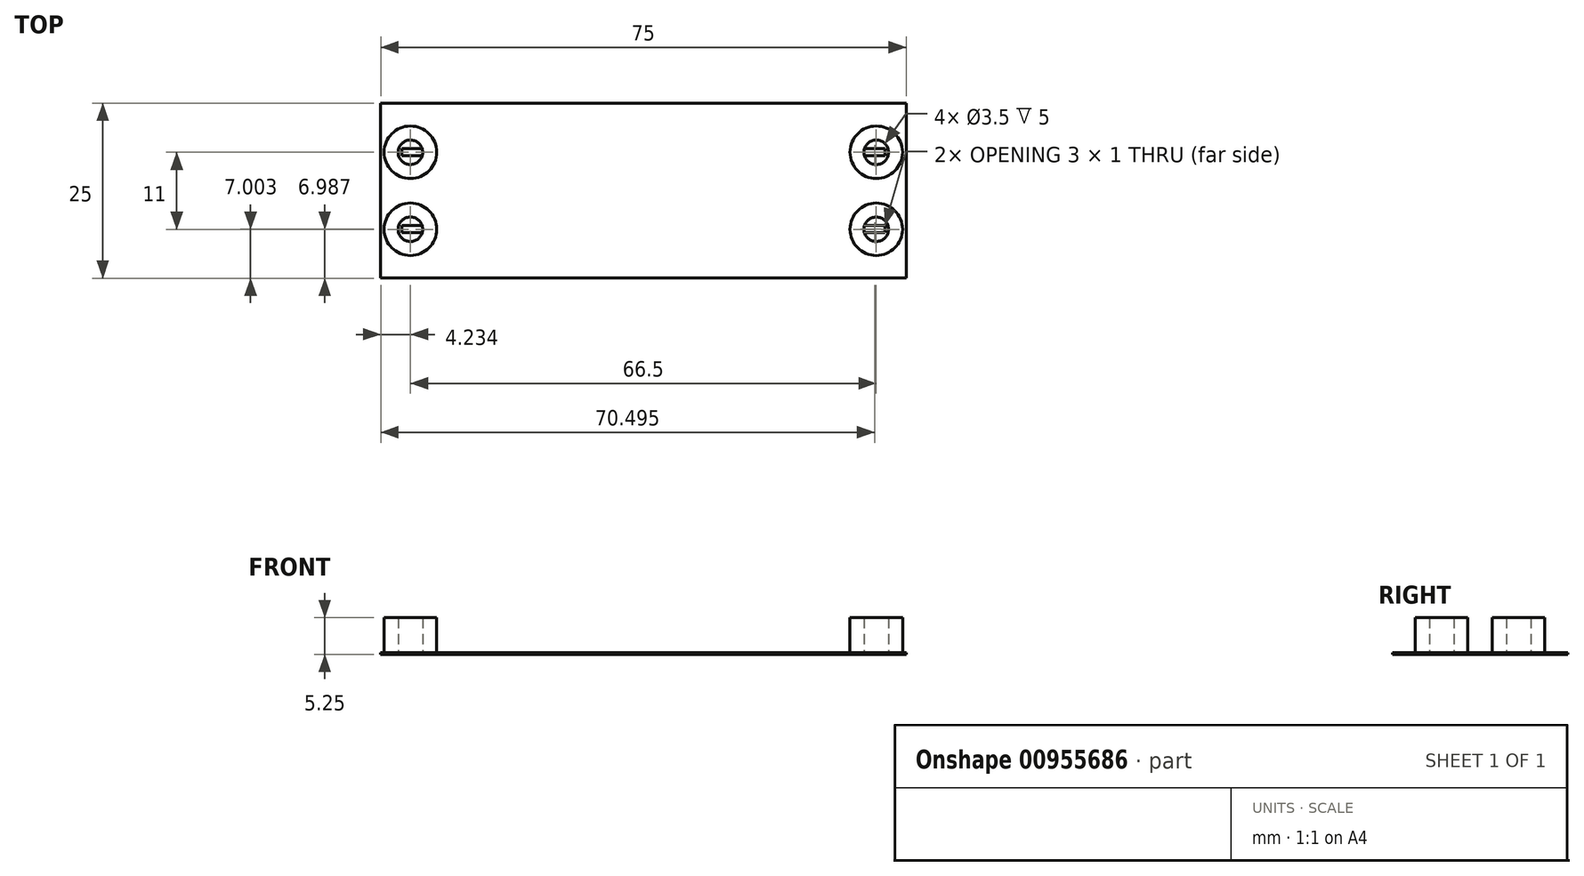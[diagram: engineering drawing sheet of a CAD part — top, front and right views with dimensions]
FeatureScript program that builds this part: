
annotation { "Feature Type Name" : "Feature", "Feature Type Description" : "" }
export const myFeature = defineFeature(function(context is Context, id is Id, definition is map)
    precondition{}
    {
        {
            var Q0;
            Q0=qCreatedBy(makeId("Top.planeOp"),FACE);
            var sketch = newSketch(context, id + "F0", { "sketchPlane" : qUnion([Q0])});
            skLineSegment(sketch, "E0.bottom", {"start": v(-37.84, 12.57) * mm, "end": v(37.16, 12.57) * mm});
            skLineSegment(sketch, "E0.top", {"start": v(-37.84, -12.43) * mm, "end": v(37.16, -12.43) * mm});
            skLineSegment(sketch, "E0.left", {"start": v(-37.84, 12.57) * mm, "end": v(-37.84, -12.43) * mm});
            skLineSegment(sketch, "E0.right", {"start": v(37.16, 12.57) * mm, "end": v(37.16, -12.43) * mm});
            skPoint(sketch, "E1", {"position": v(37.16, 0.07) * mm});
            skPoint(sketch, "E2", {"position": v(-37.84, 0.07) * mm});
            skPoint(sketch, "E3", {"position": v(-37.84, 5.57) * mm});
            skPoint(sketch, "E4", {"position": v(-37.84, -5.43) * mm});
            skPoint(sketch, "E5", {"position": v(37.16, 5.57) * mm});
            skPoint(sketch, "E6", {"position": v(37.16, -5.43) * mm});
            skPoint(sketch, "E7", {"position": v(-34.84, 5.57) * mm});
            skPoint(sketch, "E8", {"position": v(-28.34, 5.57) * mm});
            skPoint(sketch, "E9", {"position": v(-34.84, -5.43) * mm});
            skPoint(sketch, "E10", {"position": v(-28.34, -5.43) * mm});
            skPoint(sketch, "E11", {"position": v(-24.34, 5.57) * mm});
            skPoint(sketch, "E12", {"position": v(-24.34, -5.43) * mm});
            skPoint(sketch, "E13", {"position": v(34.16, 5.57) * mm});
            skPoint(sketch, "E14", {"position": v(27.66, 5.57) * mm});
            skPoint(sketch, "E15", {"position": v(23.66, 5.57) * mm});
            skPoint(sketch, "E16", {"position": v(34.16, -5.43) * mm});
            skPoint(sketch, "E17", {"position": v(27.66, -5.43) * mm});
            skPoint(sketch, "E18", {"position": v(23.66, -5.43) * mm});
            skPoint(sketch, "E19", {"position": v(-34.84, 6.07) * mm});
            skPoint(sketch, "E20", {"position": v(-34.84, 5.07) * mm});
            skPoint(sketch, "E21", {"position": v(-28.34, 5.07) * mm});
            skPoint(sketch, "E22", {"position": v(-28.34, 6.07) * mm});
            skPoint(sketch, "E23", {"position": v(-24.34, 9.57) * mm});
            skPoint(sketch, "E24", {"position": v(-24.34, 1.57) * mm});
            skPoint(sketch, "E25", {"position": v(-34.84, -4.93) * mm});
            skPoint(sketch, "E26", {"position": v(-34.84, -5.93) * mm});
            skPoint(sketch, "E27", {"position": v(-28.34, -5.93) * mm});
            skPoint(sketch, "E28", {"position": v(-28.34, -4.93) * mm});
            skPoint(sketch, "E29", {"position": v(-24.34, -1.43) * mm});
            skPoint(sketch, "E30", {"position": v(-24.34, -9.43) * mm});
            skPoint(sketch, "E31", {"position": v(34.16, -4.93) * mm});
            skPoint(sketch, "E32", {"position": v(34.16, -5.93) * mm});
            skPoint(sketch, "E33", {"position": v(27.66, -4.93) * mm});
            skPoint(sketch, "E34", {"position": v(27.66, -5.93) * mm});
            skPoint(sketch, "E35", {"position": v(23.66, -1.43) * mm});
            skPoint(sketch, "E36", {"position": v(23.66, -9.43) * mm});
            skPoint(sketch, "E37", {"position": v(34.16, 6.07) * mm});
            skPoint(sketch, "E38", {"position": v(34.16, 5.07) * mm});
            skPoint(sketch, "E39", {"position": v(27.66, 6.07) * mm});
            skPoint(sketch, "E40", {"position": v(27.66, 5.07) * mm});
            skPoint(sketch, "E41", {"position": v(23.66, 9.57) * mm});
            skPoint(sketch, "E42", {"position": v(23.66, 1.57) * mm});
            skLineSegment(sketch, "E43", {"start": v(-34.84, 6.07) * mm, "end": v(-28.34, 6.07) * mm});
            skLineSegment(sketch, "E44", {"start": v(-28.34, 6.07) * mm, "end": v(-24.34, 9.57) * mm});
            skLineSegment(sketch, "E45", {"start": v(-34.84, 6.07) * mm, "end": v(-34.84, 5.07) * mm});
            skLineSegment(sketch, "E46", {"start": v(-34.84, 5.07) * mm, "end": v(-28.34, 5.07) * mm});
            skLineSegment(sketch, "E47", {"start": v(-28.34, 5.07) * mm, "end": v(-24.34, 1.57) * mm});
            skLineSegment(sketch, "E48", {"start": v(-24.34, 9.57) * mm, "end": v(23.66, 9.57) * mm});
            skLineSegment(sketch, "E49", {"start": v(-24.34, 1.57) * mm, "end": v(23.66, 1.57) * mm});
            skLineSegment(sketch, "E50", {"start": v(23.66, 9.57) * mm, "end": v(27.66, 6.07) * mm});
            skLineSegment(sketch, "E51", {"start": v(27.66, 6.07) * mm, "end": v(34.16, 6.07) * mm});
            skLineSegment(sketch, "E52", {"start": v(34.16, 6.07) * mm, "end": v(34.16, 5.07) * mm});
            skLineSegment(sketch, "E53", {"start": v(34.16, 5.07) * mm, "end": v(27.66, 5.07) * mm});
            skLineSegment(sketch, "E54", {"start": v(27.66, 5.07) * mm, "end": v(23.66, 1.57) * mm});
            skLineSegment(sketch, "E55", {"start": v(-34.84, -4.93) * mm, "end": v(-28.34, -4.93) * mm});
            skLineSegment(sketch, "E56", {"start": v(-28.34, -4.93) * mm, "end": v(-24.34, -1.43) * mm});
            skLineSegment(sketch, "E57", {"start": v(-34.84, -4.93) * mm, "end": v(-34.84, -5.93) * mm});
            skLineSegment(sketch, "E58", {"start": v(-34.84, -5.93) * mm, "end": v(-28.34, -5.93) * mm});
            skLineSegment(sketch, "E59", {"start": v(-28.34, -5.93) * mm, "end": v(-24.34, -9.43) * mm});
            skLineSegment(sketch, "E60", {"start": v(-24.34, -1.43) * mm, "end": v(23.66, -1.43) * mm});
            skLineSegment(sketch, "E61", {"start": v(-24.34, -9.43) * mm, "end": v(23.66, -9.43) * mm});
            skLineSegment(sketch, "E62", {"start": v(23.66, -1.43) * mm, "end": v(27.66, -4.93) * mm});
            skLineSegment(sketch, "E63", {"start": v(27.66, -4.93) * mm, "end": v(34.16, -4.93) * mm});
            skLineSegment(sketch, "E64", {"start": v(34.16, -4.93) * mm, "end": v(34.16, -5.93) * mm});
            skLineSegment(sketch, "E65", {"start": v(34.16, -5.93) * mm, "end": v(27.66, -5.93) * mm});
            skLineSegment(sketch, "E66", {"start": v(27.66, -5.93) * mm, "end": v(23.66, -9.43) * mm});
            skPoint(sketch, "E67", {"position": v(-33.6, 5.57) * mm});
            skCircle(sketch, "E68", {"center": v(-33.6, 5.57) * mm, "radius": 3.75 * mm});
            skPoint(sketch, "E69", {"position": v(-33.6, -5.43) * mm});
            skCircle(sketch, "E70", {"center": v(-33.6, -5.43) * mm, "radius": 3.75 * mm});
            skPoint(sketch, "E71", {"position": v(32.9, 5.57) * mm});
            skPoint(sketch, "E72", {"position": v(32.9, -5.43) * mm});
            skCircle(sketch, "E73", {"center": v(32.9, 5.57) * mm, "radius": 3.75 * mm});
            skCircle(sketch, "E74", {"center": v(32.9, -5.43) * mm, "radius": 3.75 * mm});
            skCircle(sketch, "E75", {"center": v(-33.6, 5.57) * mm, "radius": 1.75 * mm});
            skCircle(sketch, "E76", {"center": v(-33.6, -5.43) * mm, "radius": 1.75 * mm});
            skCircle(sketch, "E77", {"center": v(32.9, 5.57) * mm, "radius": 1.75 * mm});
            skCircle(sketch, "E78", {"center": v(32.9, -5.43) * mm, "radius": 1.75 * mm});
            skPoint(sketch, "E79", {"position": v(-12.34, 9.57) * mm});
            skPoint(sketch, "E80", {"position": v(-12.34, 1.57) * mm});
            skPoint(sketch, "E81", {"position": v(11.66, 9.57) * mm});
            skPoint(sketch, "E82", {"position": v(11.66, 1.57) * mm});
            skPoint(sketch, "E83", {"position": v(-12.34, -1.43) * mm});
            skPoint(sketch, "E84", {"position": v(-12.34, -9.43) * mm});
            skPoint(sketch, "E85", {"position": v(11.66, -1.43) * mm});
            skPoint(sketch, "E86", {"position": v(11.66, -9.43) * mm});
            skLineSegment(sketch, "E87", {"start": v(-28.34, 6.07) * mm, "end": v(-28.34, 5.07) * mm});
            skLineSegment(sketch, "E88", {"start": v(-28.34, -4.93) * mm, "end": v(-28.34, -5.93) * mm});
            skLineSegment(sketch, "E89", {"start": v(27.66, -4.93) * mm, "end": v(27.66, -5.93) * mm});
            skLineSegment(sketch, "E90", {"start": v(27.66, 6.07) * mm, "end": v(27.66, 5.07) * mm});
            skSolve(sketch);
        }
        {
            var Q0;
            Q0=makeQuery(id+"F0.imprint","IMPRINT",FACE,{"disambiguationData":[TD([[makeQuery(id+"F0.imprint","IMPRINT",EDGE,{"derivedFrom":sQuery(id+"F0.wireOp",EDGE,"E0.bottom")}),-1.0]])]});
            var Q1;
            {var subQ0=sQuery(id+"F0.wireOp",EDGE,"E90");Q1=makeQuery(id+"F0.imprint","IMPRINT",FACE,{"disambiguationData":[TD([[makeQuery(id+"F0.imprint","IMPRINT",EDGE,{"derivedFrom":subQ0}),1.0]])]});}
            var Q2;
            {var subQ0=sQuery(id+"F0.wireOp",EDGE,"E73");var subQ1=sQuery(id+"F0.wireOp",EDGE,"E51");var subQ2=makeQuery(id+"F0.imprint","INTERSECT",VERTEX,{"derivedFrom":[subQ1,subQ0]});Q2=makeQuery(id+"F0.imprint","IMPRINT",FACE,{"disambiguationData":[TD([[makeQuery(id+"F0.imprint","IMPRINT",EDGE,{"disambiguationData":[TD([[subQ2,-1.0]])],"derivedFrom":subQ1}),1.0]])]});}
            var Q3;
            {var subQ0=sQuery(id+"F0.wireOp",EDGE,"E73");var subQ1=sQuery(id+"F0.wireOp",EDGE,"E51");var subQ2=makeQuery(id+"F0.imprint","INTERSECT",VERTEX,{"derivedFrom":[subQ1,subQ0]});Q3=makeQuery(id+"F0.imprint","IMPRINT",FACE,{"disambiguationData":[TD([[makeQuery(id+"F0.imprint","IMPRINT",EDGE,{"disambiguationData":[TD([[subQ2,-1.0]])],"derivedFrom":subQ1}),-1.0]])]});}
            var Q4;
            {var subQ0=sQuery(id+"F0.wireOp",EDGE,"E52");Q4=makeQuery(id+"F0.imprint","IMPRINT",FACE,{"disambiguationData":[TD([[makeQuery(id+"F0.imprint","IMPRINT",EDGE,{"derivedFrom":subQ0}),1.0]])]});}
            var Q5;
            {var subQ0=sQuery(id+"F0.wireOp",EDGE,"E89");Q5=makeQuery(id+"F0.imprint","IMPRINT",FACE,{"disambiguationData":[TD([[makeQuery(id+"F0.imprint","IMPRINT",EDGE,{"derivedFrom":subQ0}),1.0]])]});}
            var Q6;
            {var subQ0=sQuery(id+"F0.wireOp",EDGE,"E74");var subQ1=sQuery(id+"F0.wireOp",EDGE,"E63");var subQ2=makeQuery(id+"F0.imprint","INTERSECT",VERTEX,{"derivedFrom":[subQ1,subQ0]});Q6=makeQuery(id+"F0.imprint","IMPRINT",FACE,{"disambiguationData":[TD([[makeQuery(id+"F0.imprint","IMPRINT",EDGE,{"disambiguationData":[TD([[subQ2,-1.0]])],"derivedFrom":subQ1}),-1.0]])]});}
            var Q7;
            {var subQ0=sQuery(id+"F0.wireOp",EDGE,"E74");var subQ1=sQuery(id+"F0.wireOp",EDGE,"E63");var subQ2=makeQuery(id+"F0.imprint","INTERSECT",VERTEX,{"derivedFrom":[subQ1,subQ0]});Q7=makeQuery(id+"F0.imprint","IMPRINT",FACE,{"disambiguationData":[TD([[makeQuery(id+"F0.imprint","IMPRINT",EDGE,{"disambiguationData":[TD([[subQ2,-1.0]])],"derivedFrom":subQ1}),1.0]])]});}
            var Q8;
            {var subQ0=sQuery(id+"F0.wireOp",EDGE,"E64");Q8=makeQuery(id+"F0.imprint","IMPRINT",FACE,{"disambiguationData":[TD([[makeQuery(id+"F0.imprint","IMPRINT",EDGE,{"derivedFrom":subQ0}),1.0]])]});}
            var Q9;
            Q9=makeQuery(id+"F0.imprint","IMPRINT",FACE,{"disambiguationData":[TD([[makeQuery(id+"F0.imprint","IMPRINT",EDGE,{"derivedFrom":sQuery(id+"F0.wireOp",EDGE,"E56")}),-1.0]])]});
            var Q10;
            Q10=makeQuery(id+"F0.imprint","IMPRINT",FACE,{"disambiguationData":[TD([[makeQuery(id+"F0.imprint","IMPRINT",EDGE,{"derivedFrom":sQuery(id+"F0.wireOp",EDGE,"E44")}),-1.0]])]});
            var Q11;
            {var subQ0=sQuery(id+"F0.wireOp",EDGE,"E87");Q11=makeQuery(id+"F0.imprint","IMPRINT",FACE,{"disambiguationData":[TD([[makeQuery(id+"F0.imprint","IMPRINT",EDGE,{"derivedFrom":subQ0}),-1.0]])]});}
            var Q12;
            {var subQ0=sQuery(id+"F0.wireOp",EDGE,"E88");Q12=makeQuery(id+"F0.imprint","IMPRINT",FACE,{"disambiguationData":[TD([[makeQuery(id+"F0.imprint","IMPRINT",EDGE,{"derivedFrom":subQ0}),-1.0]])]});}
            var Q13;
            {var subQ0=sQuery(id+"F0.wireOp",EDGE,"E76");var subQ1=sQuery(id+"F0.wireOp",EDGE,"E55");var subQ2=makeQuery(id+"F0.imprint","INTERSECT",VERTEX,{"derivedFrom":[subQ1,subQ0]});Q13=makeQuery(id+"F0.imprint","IMPRINT",FACE,{"disambiguationData":[TD([[makeQuery(id+"F0.imprint","IMPRINT",EDGE,{"disambiguationData":[TD([[subQ2,-1.0]])],"derivedFrom":subQ1}),1.0]])]});}
            var Q14;
            {var subQ0=sQuery(id+"F0.wireOp",EDGE,"E76");var subQ1=sQuery(id+"F0.wireOp",EDGE,"E55");var subQ2=makeQuery(id+"F0.imprint","INTERSECT",VERTEX,{"derivedFrom":[subQ1,subQ0]});Q14=makeQuery(id+"F0.imprint","IMPRINT",FACE,{"disambiguationData":[TD([[makeQuery(id+"F0.imprint","IMPRINT",EDGE,{"disambiguationData":[TD([[subQ2,-1.0]])],"derivedFrom":subQ1}),-1.0]])]});}
            var Q15;
            {var subQ0=sQuery(id+"F0.wireOp",EDGE,"E57");Q15=makeQuery(id+"F0.imprint","IMPRINT",FACE,{"disambiguationData":[TD([[makeQuery(id+"F0.imprint","IMPRINT",EDGE,{"derivedFrom":subQ0}),-1.0]])]});}
            var Q16;
            {var subQ0=sQuery(id+"F0.wireOp",EDGE,"E75");var subQ1=sQuery(id+"F0.wireOp",EDGE,"E43");var subQ2=makeQuery(id+"F0.imprint","INTERSECT",VERTEX,{"derivedFrom":[subQ1,subQ0]});Q16=makeQuery(id+"F0.imprint","IMPRINT",FACE,{"disambiguationData":[TD([[makeQuery(id+"F0.imprint","IMPRINT",EDGE,{"disambiguationData":[TD([[subQ2,-1.0]])],"derivedFrom":subQ1}),1.0]])]});}
            var Q17;
            {var subQ0=sQuery(id+"F0.wireOp",EDGE,"E75");var subQ1=sQuery(id+"F0.wireOp",EDGE,"E43");var subQ2=makeQuery(id+"F0.imprint","INTERSECT",VERTEX,{"derivedFrom":[subQ1,subQ0]});Q17=makeQuery(id+"F0.imprint","IMPRINT",FACE,{"disambiguationData":[TD([[makeQuery(id+"F0.imprint","IMPRINT",EDGE,{"disambiguationData":[TD([[subQ2,-1.0]])],"derivedFrom":subQ1}),-1.0]])]});}
            var Q18;
            {var subQ0=sQuery(id+"F0.wireOp",EDGE,"E45");Q18=makeQuery(id+"F0.imprint","IMPRINT",FACE,{"disambiguationData":[TD([[makeQuery(id+"F0.imprint","IMPRINT",EDGE,{"derivedFrom":subQ0}),-1.0]])]});}
            extrude(context, id + "F1", {"entities" : qUnion([Q0, Q1, Q2, Q3, Q4, Q5, Q6, Q7, Q8, Q9, Q10, Q11, Q12, Q13, Q14, Q15, Q16, Q17, Q18]), "depth" : 0.25 * mm, "offsetDistance" : 25 * mm});
        }
        {
            var Q0;
            Q0=qCreatedBy(makeId("Top.planeOp"),FACE);
            cPlane(context, id + "F2", {"entities" : qUnion([Q0]), "cplaneType" : CPlaneType.OFFSET, "offset" : 0.25 * mm, "width" : 150 * mm, "height" : 150 * mm});
        }
        {
            var Q0;
            Q0=qCreatedBy(id+"F2.planeOp",FACE);
            var sketch = newSketch(context, id + "F3", { "sketchPlane" : qUnion([Q0])});
            skLineSegment(sketch, "E91.bottom", {"start": v(-37.86, 12.56) * mm, "end": v(37.14, 12.56) * mm});
            skLineSegment(sketch, "E91.top", {"start": v(-37.86, -12.44) * mm, "end": v(37.14, -12.44) * mm});
            skLineSegment(sketch, "E91.left", {"start": v(-37.86, 12.56) * mm, "end": v(-37.86, -12.44) * mm});
            skLineSegment(sketch, "E91.right", {"start": v(37.14, 12.56) * mm, "end": v(37.14, -12.44) * mm});
            skPoint(sketch, "E92", {"position": v(37.14, 0.06) * mm});
            skPoint(sketch, "E93", {"position": v(-37.86, 0.06) * mm});
            skPoint(sketch, "E94", {"position": v(-37.86, 5.56) * mm});
            skPoint(sketch, "E95", {"position": v(-37.86, -5.44) * mm});
            skPoint(sketch, "E96", {"position": v(37.14, 5.56) * mm});
            skPoint(sketch, "E97", {"position": v(37.14, -5.44) * mm});
            skPoint(sketch, "E98", {"position": v(-34.86, 5.56) * mm});
            skPoint(sketch, "E99", {"position": v(-28.36, 5.56) * mm});
            skPoint(sketch, "E100", {"position": v(-34.86, -5.44) * mm});
            skPoint(sketch, "E101", {"position": v(-28.36, -5.44) * mm});
            skPoint(sketch, "E102", {"position": v(-24.36, 5.56) * mm});
            skPoint(sketch, "E103", {"position": v(-24.36, -5.44) * mm});
            skPoint(sketch, "E104", {"position": v(34.14, 5.56) * mm});
            skPoint(sketch, "E105", {"position": v(27.64, 5.56) * mm});
            skPoint(sketch, "E106", {"position": v(23.64, 5.56) * mm});
            skPoint(sketch, "E107", {"position": v(34.14, -5.44) * mm});
            skPoint(sketch, "E108", {"position": v(27.64, -5.44) * mm});
            skPoint(sketch, "E109", {"position": v(23.64, -5.44) * mm});
            skPoint(sketch, "E110", {"position": v(-34.86, 6.06) * mm});
            skPoint(sketch, "E111", {"position": v(-34.86, 5.06) * mm});
            skPoint(sketch, "E112", {"position": v(-28.36, 5.06) * mm});
            skPoint(sketch, "E113", {"position": v(-28.36, 6.06) * mm});
            skPoint(sketch, "E114", {"position": v(-24.36, 9.56) * mm});
            skPoint(sketch, "E115", {"position": v(-24.36, 1.56) * mm});
            skPoint(sketch, "E116", {"position": v(-34.86, -4.94) * mm});
            skPoint(sketch, "E117", {"position": v(-34.86, -5.94) * mm});
            skPoint(sketch, "E118", {"position": v(-28.36, -5.94) * mm});
            skPoint(sketch, "E119", {"position": v(-28.36, -4.94) * mm});
            skPoint(sketch, "E120", {"position": v(-24.36, -1.44) * mm});
            skPoint(sketch, "E121", {"position": v(-24.36, -9.44) * mm});
            skPoint(sketch, "E122", {"position": v(34.14, -4.94) * mm});
            skPoint(sketch, "E123", {"position": v(34.14, -5.94) * mm});
            skPoint(sketch, "E124", {"position": v(27.64, -4.94) * mm});
            skPoint(sketch, "E125", {"position": v(27.64, -5.94) * mm});
            skPoint(sketch, "E126", {"position": v(23.64, -1.44) * mm});
            skPoint(sketch, "E127", {"position": v(23.64, -9.44) * mm});
            skPoint(sketch, "E128", {"position": v(34.14, 6.06) * mm});
            skPoint(sketch, "E129", {"position": v(34.14, 5.06) * mm});
            skPoint(sketch, "E130", {"position": v(27.64, 6.06) * mm});
            skPoint(sketch, "E131", {"position": v(27.64, 5.06) * mm});
            skPoint(sketch, "E132", {"position": v(23.64, 9.56) * mm});
            skPoint(sketch, "E133", {"position": v(23.64, 1.56) * mm});
            skLineSegment(sketch, "E134", {"start": v(-34.86, 6.06) * mm, "end": v(-28.36, 6.06) * mm});
            skLineSegment(sketch, "E135", {"start": v(-28.36, 6.06) * mm, "end": v(-24.36, 9.56) * mm});
            skLineSegment(sketch, "E136", {"start": v(-34.86, 6.06) * mm, "end": v(-34.86, 5.06) * mm});
            skLineSegment(sketch, "E137", {"start": v(-34.86, 5.06) * mm, "end": v(-28.36, 5.06) * mm});
            skLineSegment(sketch, "E138", {"start": v(-28.36, 5.06) * mm, "end": v(-24.36, 1.56) * mm});
            skLineSegment(sketch, "E139", {"start": v(-24.36, 9.56) * mm, "end": v(23.64, 9.56) * mm});
            skLineSegment(sketch, "E140", {"start": v(-24.36, 1.56) * mm, "end": v(23.64, 1.56) * mm});
            skLineSegment(sketch, "E141", {"start": v(23.64, 9.56) * mm, "end": v(27.64, 6.06) * mm});
            skLineSegment(sketch, "E142", {"start": v(27.64, 6.06) * mm, "end": v(34.14, 6.06) * mm});
            skLineSegment(sketch, "E143", {"start": v(34.14, 6.06) * mm, "end": v(34.14, 5.06) * mm});
            skLineSegment(sketch, "E144", {"start": v(34.14, 5.06) * mm, "end": v(27.64, 5.06) * mm});
            skLineSegment(sketch, "E145", {"start": v(27.64, 5.06) * mm, "end": v(23.64, 1.56) * mm});
            skLineSegment(sketch, "E146", {"start": v(-34.86, -4.94) * mm, "end": v(-28.36, -4.94) * mm});
            skLineSegment(sketch, "E147", {"start": v(-28.36, -4.94) * mm, "end": v(-24.36, -1.44) * mm});
            skLineSegment(sketch, "E148", {"start": v(-34.86, -4.94) * mm, "end": v(-34.86, -5.94) * mm});
            skLineSegment(sketch, "E149", {"start": v(-34.86, -5.94) * mm, "end": v(-28.36, -5.94) * mm});
            skLineSegment(sketch, "E150", {"start": v(-28.36, -5.94) * mm, "end": v(-24.36, -9.44) * mm});
            skLineSegment(sketch, "E151", {"start": v(-24.36, -1.44) * mm, "end": v(23.64, -1.44) * mm});
            skLineSegment(sketch, "E152", {"start": v(-24.36, -9.44) * mm, "end": v(23.64, -9.44) * mm});
            skLineSegment(sketch, "E153", {"start": v(23.64, -1.44) * mm, "end": v(27.64, -4.94) * mm});
            skLineSegment(sketch, "E154", {"start": v(27.64, -4.94) * mm, "end": v(34.14, -4.94) * mm});
            skLineSegment(sketch, "E155", {"start": v(34.14, -4.94) * mm, "end": v(34.14, -5.94) * mm});
            skLineSegment(sketch, "E156", {"start": v(34.14, -5.94) * mm, "end": v(27.64, -5.94) * mm});
            skLineSegment(sketch, "E157", {"start": v(27.64, -5.94) * mm, "end": v(23.64, -9.44) * mm});
            skPoint(sketch, "E158", {"position": v(-33.6, 5.56) * mm});
            skCircle(sketch, "E159", {"center": v(-33.6, 5.56) * mm, "radius": 3.75 * mm});
            skPoint(sketch, "E160", {"position": v(-33.6, -5.44) * mm});
            skCircle(sketch, "E161", {"center": v(-33.6, -5.44) * mm, "radius": 3.75 * mm});
            skPoint(sketch, "E162", {"position": v(32.9, 5.56) * mm});
            skPoint(sketch, "E163", {"position": v(32.9, -5.44) * mm});
            skCircle(sketch, "E164", {"center": v(32.9, 5.56) * mm, "radius": 3.75 * mm});
            skCircle(sketch, "E165", {"center": v(32.9, -5.44) * mm, "radius": 3.75 * mm});
            skCircle(sketch, "E166", {"center": v(-33.6, 5.56) * mm, "radius": 1.75 * mm});
            skCircle(sketch, "E167", {"center": v(-33.6, -5.44) * mm, "radius": 1.75 * mm});
            skCircle(sketch, "E168", {"center": v(32.9, 5.56) * mm, "radius": 1.75 * mm});
            skCircle(sketch, "E169", {"center": v(32.9, -5.44) * mm, "radius": 1.75 * mm});
            skPoint(sketch, "E170", {"position": v(-12.36, 9.56) * mm});
            skPoint(sketch, "E171", {"position": v(-12.36, 1.56) * mm});
            skPoint(sketch, "E172", {"position": v(11.64, 9.56) * mm});
            skPoint(sketch, "E173", {"position": v(11.64, 1.56) * mm});
            skPoint(sketch, "E174", {"position": v(-12.36, -1.44) * mm});
            skPoint(sketch, "E175", {"position": v(-12.36, -9.44) * mm});
            skPoint(sketch, "E176", {"position": v(11.64, -1.44) * mm});
            skPoint(sketch, "E177", {"position": v(11.64, -9.44) * mm});
            skLineSegment(sketch, "E178", {"start": v(-28.36, 6.06) * mm, "end": v(-28.36, 5.06) * mm});
            skLineSegment(sketch, "E179", {"start": v(-28.36, -4.94) * mm, "end": v(-28.36, -5.94) * mm});
            skLineSegment(sketch, "E180", {"start": v(27.64, -4.94) * mm, "end": v(27.64, -5.94) * mm});
            skLineSegment(sketch, "E181", {"start": v(27.64, 6.06) * mm, "end": v(27.64, 5.06) * mm});
            skSolve(sketch);
        }
        {
            var Q0;
            {var subQ0=sQuery(id+"F3.wireOp",EDGE,"E164");var subQ1=sQuery(id+"F3.wireOp",EDGE,"E142");var subQ2=makeQuery(id+"F3.imprint","INTERSECT",VERTEX,{"derivedFrom":[subQ1,subQ0]});Q0=makeQuery(id+"F3.imprint","IMPRINT",FACE,{"disambiguationData":[TD([[makeQuery(id+"F3.imprint","IMPRINT",EDGE,{"disambiguationData":[TD([[subQ2,-1.0]])],"derivedFrom":subQ1}),1.0]])]});}
            var Q1;
            {var subQ0=sQuery(id+"F3.wireOp",EDGE,"E164");var subQ1=sQuery(id+"F3.wireOp",EDGE,"E142");var subQ2=makeQuery(id+"F3.imprint","INTERSECT",VERTEX,{"derivedFrom":[subQ1,subQ0]});Q1=makeQuery(id+"F3.imprint","IMPRINT",FACE,{"disambiguationData":[TD([[makeQuery(id+"F3.imprint","IMPRINT",EDGE,{"disambiguationData":[TD([[subQ2,-1.0]])],"derivedFrom":subQ1}),-1.0]])]});}
            var Q2;
            {var subQ0=sQuery(id+"F3.wireOp",EDGE,"E165");var subQ1=sQuery(id+"F3.wireOp",EDGE,"E154");var subQ2=makeQuery(id+"F3.imprint","INTERSECT",VERTEX,{"derivedFrom":[subQ1,subQ0]});Q2=makeQuery(id+"F3.imprint","IMPRINT",FACE,{"disambiguationData":[TD([[makeQuery(id+"F3.imprint","IMPRINT",EDGE,{"disambiguationData":[TD([[subQ2,-1.0]])],"derivedFrom":subQ1}),1.0]])]});}
            var Q3;
            {var subQ0=sQuery(id+"F3.wireOp",EDGE,"E165");var subQ1=sQuery(id+"F3.wireOp",EDGE,"E154");var subQ2=makeQuery(id+"F3.imprint","INTERSECT",VERTEX,{"derivedFrom":[subQ1,subQ0]});Q3=makeQuery(id+"F3.imprint","IMPRINT",FACE,{"disambiguationData":[TD([[makeQuery(id+"F3.imprint","IMPRINT",EDGE,{"disambiguationData":[TD([[subQ2,-1.0]])],"derivedFrom":subQ1}),-1.0]])]});}
            var Q4;
            {var subQ0=sQuery(id+"F3.wireOp",EDGE,"E166");var subQ1=sQuery(id+"F3.wireOp",EDGE,"E134");var subQ2=makeQuery(id+"F3.imprint","INTERSECT",VERTEX,{"derivedFrom":[subQ1,subQ0]});Q4=makeQuery(id+"F3.imprint","IMPRINT",FACE,{"disambiguationData":[TD([[makeQuery(id+"F3.imprint","IMPRINT",EDGE,{"disambiguationData":[TD([[subQ2,-1.0]])],"derivedFrom":subQ1}),1.0]])]});}
            var Q5;
            {var subQ0=sQuery(id+"F3.wireOp",EDGE,"E166");var subQ1=sQuery(id+"F3.wireOp",EDGE,"E134");var subQ2=makeQuery(id+"F3.imprint","INTERSECT",VERTEX,{"derivedFrom":[subQ1,subQ0]});Q5=makeQuery(id+"F3.imprint","IMPRINT",FACE,{"disambiguationData":[TD([[makeQuery(id+"F3.imprint","IMPRINT",EDGE,{"disambiguationData":[TD([[subQ2,-1.0]])],"derivedFrom":subQ1}),-1.0]])]});}
            var Q6;
            {var subQ0=sQuery(id+"F3.wireOp",EDGE,"E167");var subQ1=sQuery(id+"F3.wireOp",EDGE,"E146");var subQ2=makeQuery(id+"F3.imprint","INTERSECT",VERTEX,{"derivedFrom":[subQ1,subQ0]});Q6=makeQuery(id+"F3.imprint","IMPRINT",FACE,{"disambiguationData":[TD([[makeQuery(id+"F3.imprint","IMPRINT",EDGE,{"disambiguationData":[TD([[subQ2,-1.0]])],"derivedFrom":subQ1}),1.0]])]});}
            var Q7;
            {var subQ0=sQuery(id+"F3.wireOp",EDGE,"E167");var subQ1=sQuery(id+"F3.wireOp",EDGE,"E146");var subQ2=makeQuery(id+"F3.imprint","INTERSECT",VERTEX,{"derivedFrom":[subQ1,subQ0]});Q7=makeQuery(id+"F3.imprint","IMPRINT",FACE,{"disambiguationData":[TD([[makeQuery(id+"F3.imprint","IMPRINT",EDGE,{"disambiguationData":[TD([[subQ2,-1.0]])],"derivedFrom":subQ1}),-1.0]])]});}
            extrude(context, id + "F4", {"entities" : qUnion([Q0, Q1, Q2, Q3, Q4, Q5, Q6, Q7]), "operationType" : NewBodyOperationType.ADD, "depth" : 5 * mm, "offsetDistance" : 25 * mm});
        }
    });
